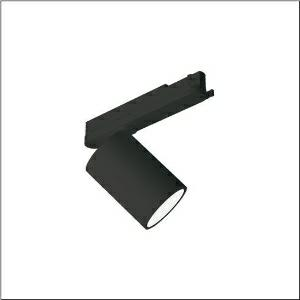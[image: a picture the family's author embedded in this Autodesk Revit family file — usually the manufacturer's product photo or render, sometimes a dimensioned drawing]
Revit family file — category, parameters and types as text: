
# Revit family: spot_31_51sf33mad4b
name_source: partatom
category: Lighting Fixtures
units: mm (PartAtom-declared; Revit-internal decimal feet)

## family parameters
Cut with Voids When Loaded = No
Host = Face
Light Source = No
Part Type = Normal
Room Calculation Point = No
Round Connector Dimension = Use Diameter
Shared = No

## types (1)
- --- (1 x LED, 5190 lm, 41.5 W, 4000K)
    Apparent Load = 42 VA
    CIE Flux Codes = 92 97 99 100 100
    Color Rendering = 90
    Color Temperature = 4000K
    Default Elevation = 1800 mm
    Description = Spot 31, directional spotlight, light control with lens, of PMMA, LED rated luminous flux: 4.980lm, light colour: 940, control gear: ECG Multilumen, with 3-phase adapter, mains connection: 220..240V, AC, 50/60Hz, of aluminium, jet black (RAL 9005), length: 213mm, diameter: 90mm, protection rating (complete): IP20, insulation class (complete): insulation class I (protective earthing), certification: CE, impact resistance: IK02, permissible ambient temperature for indoor applications: -20..+40°C, packaging unit: 1 piece
    Height = 175 mm
    Lamp = 1 x LED
    Lamp Light Flux = 5190 lm
    Lamp Power = 41.5 W
    Lamp count = 1
    Length = 90 mm
    Luminous efficacy = 125 lm/W
    Manufacturer = Siteco
    ModVariant = No
    Model = 51SF33MAD4B
    Mounting Place = Ceiling
    Mounting Type = Pendant
    Number of Poles = 1
    OnlyDefault = Yes
    Power Factor = 1
    Product Name = Spot 31
    Product group = directional spotlight
    ProductGroupID = 906
    Protection Class = Protection class I
    Protection Degree = IP 20
    RLX_Detail_Level = 1
    RLX_Emergency_Light_Flux = 0 lm
    RLX_Emergency_Type = 0
    RLX_Emergency_Type_DB = No
    RlxData = <blob elided: 20889 chars, md5=5bbc0ba2>
    Socket = socket
    Standby Power = 0 W
    System Light Flux = 5190 lm
    System Power = 42 W
    Type Comments = factory setting: luminous flux: 100 % | (ON | ON | ON | ON) | 1050 mA
    Type Image = l_1273723.jpg
    URL = http://relux.com
    VarID = @adj_146410
    Voltage = 0 V
    Weight = 0.00 kg
    Width = 0 mm  [stored 0 ft]

note: [stored X ft] marks values corroborated as IEEE doubles in the binary element streams (Revit-internal decimal feet)

## geometry (parser evidence)
native form markers: Blend x4, Sweep x11
no freeform markers — native parametric forms only
